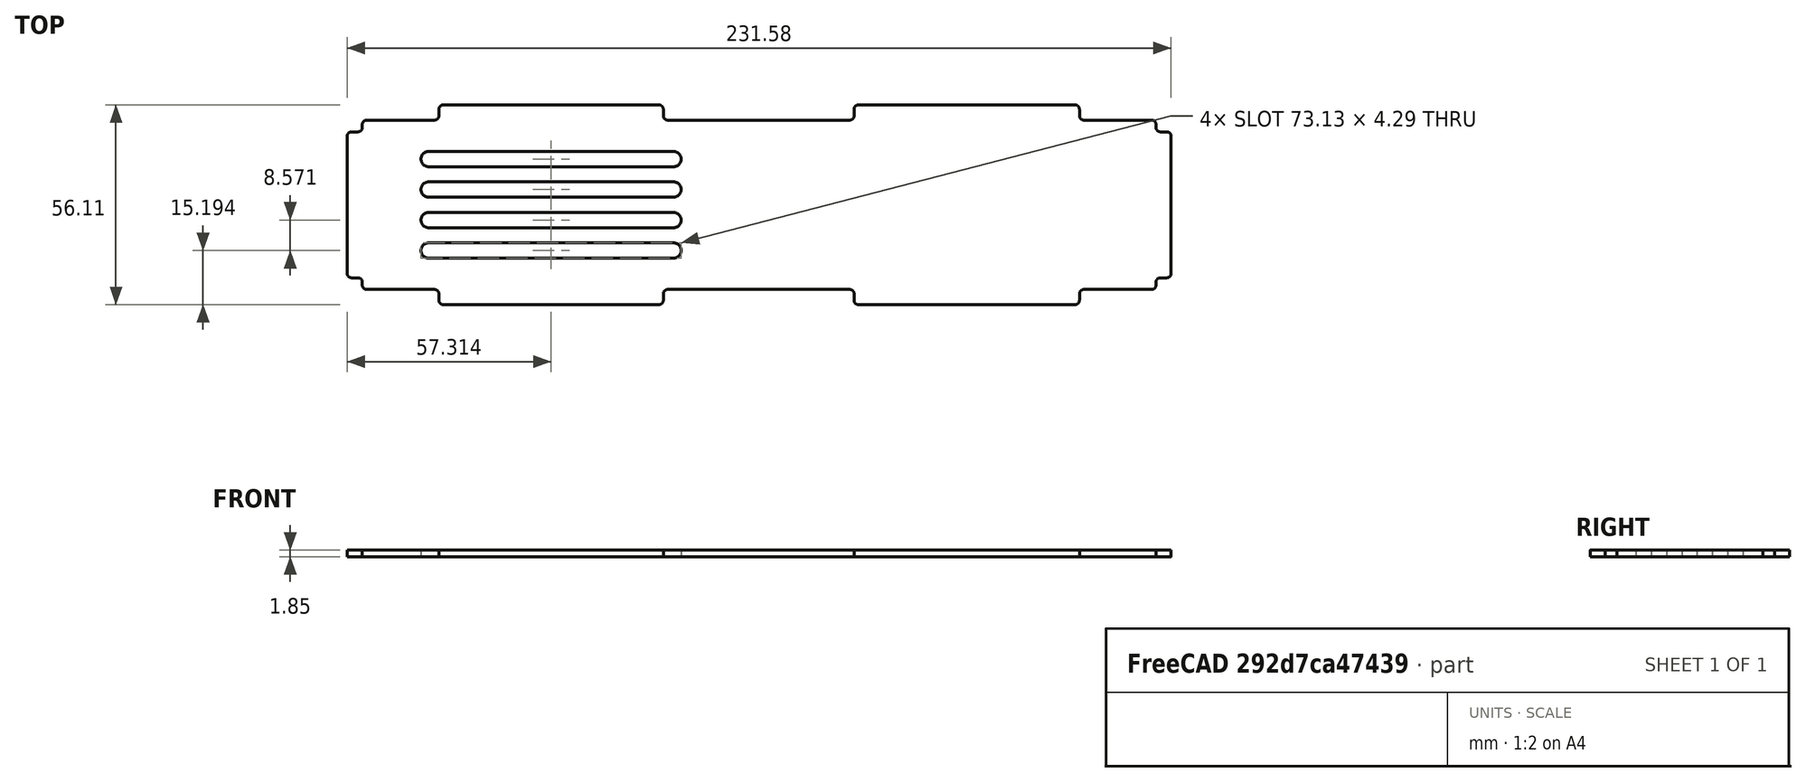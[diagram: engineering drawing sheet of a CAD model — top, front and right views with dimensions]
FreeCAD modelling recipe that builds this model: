
FCSTD DOCUMENT  (FreeCAD 1.0R38641 +468 (Git))
Label: psu_side_long
License: All rights reserved
LicenseURL: https://en.wikipedia.org/wiki/All_rights_reserved
objects: PartDesign::SubShapeBinder×2, Sketcher::SketchObject×1, PartDesign::Pad×1, PartDesign::Body×1
note: 8 computed .brp shape members not serialized (recipe doc carries the construction recipe); baked Part::Feature solids carry a one-line shape summary decoded from their .brp
EXTERNAL_REF file=../dimensions.FCStd obj=VarSet
EXTERNAL_REF file=psu_side_short.FCStd obj=Body
EXTERNAL_REF file=psu_top_and_bottom.FCStd obj=Body

FEATURE [PartDesign::SubShapeBinder] Binder  label="PsuSideShortBinderBinder"
  BindCopyOnChange = 0
  BindMode = 0
  ClaimChildren = false
  Context = -> Body [Binder.]
  Fuse = false
  MakeFace = true
  OffsetFill = false
  OffsetIntersection = false
  OffsetJoinType = 0
  OffsetOpenResult = false
  PartialLoad = false
  Placement = pos=(0.127,0,0) rot=(0,0,1;0rad)
  Refine = true
  Relative = true
  Support = -> [<external psu_side_short.FCStd>#Body]
  _Version = 2
  expr: .Placement.Base.x = dimensions#VarSet.EnclosureFinishThickness
FEATURE [PartDesign::SubShapeBinder] Binder001  label="PsuTopAndBottomBinder"
  BindCopyOnChange = 0
  BindMode = 0
  ClaimChildren = false
  Context = -> Body [Binder001.]
  Fuse = false
  MakeFace = true
  OffsetFill = false
  OffsetIntersection = false
  OffsetJoinType = 0
  OffsetOpenResult = false
  PartialLoad = false
  Refine = true
  Relative = true
  Support = -> [<external psu_top_and_bottom.FCStd>#Body]
  _Version = 2
FEATURE [Sketcher::SketchObject] Sketch
  ArcFitTolerance = 1e-06
  AttachmentSupport = -> [Binder001]
  ExternalGeometry = -> [Binder001,Binder]
  FullyConstrained = true
  MakeInternals = false
  MapMode = 5
  Placement = pos=(0,-3.1e-15,-14.1418) rot=(0,0,1;0rad)
  expr: Constraints[183] = dimensions#VarSet.EnclosureCornerRadius
  expr: Constraints[49] = dimensions#VarSet.EnclosureFinishThickness
  sketch-geometry (113):
    g0: LineSegment [constr] StartX=303.647 StartY=129.081 StartZ=0 EndX=303.52 EndY=129.081 EndZ=0
    g1: LineSegment [constr] StartX=240.305 StartY=129.081 StartZ=0 EndX=240.178 EndY=129.081 EndZ=0
    g2: LineSegment [constr] StartX=123.353 StartY=129.081 StartZ=0 EndX=123.48 EndY=129.081 EndZ=0
    g3: LineSegment [constr] StartX=186.695 StartY=129.081 StartZ=0 EndX=186.568 EndY=129.081 EndZ=0
    g4: LineSegment [constr] StartX=326.235 StartY=133.444 StartZ=0 EndX=326.235 EndY=133.571 EndZ=0
    g5: LineSegment [constr] StartX=326.235 StartY=174.719 StartZ=0 EndX=326.235 EndY=174.592 EndZ=0
    g6: LineSegment StartX=326.235 StartY=174.592 StartZ=0 EndX=328.089 EndY=174.592 EndZ=0
    g7: LineSegment StartX=329.289 StartY=173.392 StartZ=0 EndX=329.289 EndY=134.771 EndZ=0
    g8: LineSegment StartX=328.089 StartY=133.571 StartZ=0 EndX=326.235 EndY=133.571 EndZ=0
    g9: LineSegment StartX=303.52 StartY=129.081 StartZ=0 EndX=303.52 EndY=127.227 EndZ=0
    g10: LineSegment StartX=240.178 StartY=129.081 StartZ=0 EndX=240.178 EndY=127.227 EndZ=0
    g11: LineSegment StartX=241.378 StartY=126.027 StartZ=0 EndX=302.32 EndY=126.027 EndZ=0
    g12: LineSegment StartX=186.568 StartY=129.081 StartZ=0 EndX=186.568 EndY=127.227 EndZ=0
    g13: LineSegment StartX=123.48 StartY=129.081 StartZ=0 EndX=123.48 EndY=127.227 EndZ=0
    g14: LineSegment StartX=124.68 StartY=126.027 StartZ=0 EndX=185.368 EndY=126.027 EndZ=0
    g15: LineSegment StartX=240.178 StartY=179.081 StartZ=0 EndX=240.178 EndY=180.935 EndZ=0
    g16: LineSegment StartX=241.378 StartY=182.135 StartZ=0 EndX=302.32 EndY=182.135 EndZ=0
    g17: LineSegment StartX=303.52 StartY=180.935 StartZ=0 EndX=303.52 EndY=179.081 EndZ=0
    g18: LineSegment StartX=304.72 StartY=130.281 StartZ=0 EndX=323.835 EndY=130.281 EndZ=0
    g19: LineSegment StartX=325.035 StartY=131.481 StartZ=0 EndX=325.035 EndY=132.371 EndZ=0
    g20: LineSegment StartX=304.72 StartY=177.881 StartZ=0 EndX=323.835 EndY=177.881 EndZ=0
    g21: LineSegment StartX=325.035 StartY=176.681 StartZ=0 EndX=325.035 EndY=175.792 EndZ=0
    g22: LineSegment StartX=187.768 StartY=130.281 StartZ=0 EndX=238.978 EndY=130.281 EndZ=0
    g23: LineSegment StartX=122.28 StartY=130.281 StartZ=0 EndX=103.165 EndY=130.281 EndZ=0
    g24: LineSegment StartX=101.965 StartY=131.481 StartZ=0 EndX=101.965 EndY=132.371 EndZ=0
    g25: LineSegment StartX=100.765 StartY=133.571 StartZ=0 EndX=98.9106 EndY=133.571 EndZ=0
    g26: LineSegment StartX=97.7106 StartY=134.771 StartZ=0 EndX=97.7106 EndY=173.392 EndZ=0
    g27: LineSegment StartX=98.9106 StartY=174.592 StartZ=0 EndX=100.765 EndY=174.592 EndZ=0
    g28: LineSegment StartX=101.965 StartY=175.792 StartZ=0 EndX=101.965 EndY=176.681 EndZ=0
    g29: LineSegment StartX=103.165 StartY=177.881 StartZ=0 EndX=122.28 EndY=177.881 EndZ=0
    g30: LineSegment StartX=123.48 StartY=179.081 StartZ=0 EndX=123.48 EndY=180.935 EndZ=0
    g31: LineSegment StartX=124.68 StartY=182.135 StartZ=0 EndX=185.368 EndY=182.135 EndZ=0
    g32: LineSegment StartX=186.568 StartY=180.935 StartZ=0 EndX=186.568 EndY=179.081 EndZ=0
    g33: LineSegment StartX=238.978 StartY=177.881 StartZ=0 EndX=187.768 EndY=177.881 EndZ=0
    g34: ArcOfCircle CenterX=122.28 CenterY=129.081 CenterZ=0 NormalX=0 NormalY=0 NormalZ=1 AngleXU=0 Radius=1.2 StartAngle=4.2e-15 EndAngle=1.5708
    g35: ArcOfCircle CenterX=187.768 CenterY=129.081 CenterZ=0 NormalX=0 NormalY=0 NormalZ=1 AngleXU=0 Radius=1.2 StartAngle=1.5708 EndAngle=3.14159
    g36: ArcOfCircle CenterX=238.978 CenterY=129.081 CenterZ=0 NormalX=0 NormalY=0 NormalZ=1 AngleXU=0 Radius=1.2 StartAngle=2.7e-15 EndAngle=1.5708
    g37: ArcOfCircle CenterX=304.72 CenterY=129.081 CenterZ=0 NormalX=0 NormalY=0 NormalZ=1 AngleXU=0 Radius=1.2 StartAngle=1.5708 EndAngle=3.14159
    g38: ArcOfCircle CenterX=326.235 CenterY=132.371 CenterZ=0 NormalX=0 NormalY=0 NormalZ=1 AngleXU=0 Radius=1.2 StartAngle=1.5708 EndAngle=3.14159
    g39: ArcOfCircle CenterX=326.235 CenterY=175.792 CenterZ=0 NormalX=0 NormalY=0 NormalZ=1 AngleXU=0 Radius=1.2 StartAngle=3.14159 EndAngle=4.71239
    g40: ArcOfCircle CenterX=328.089 CenterY=134.771 CenterZ=0 NormalX=0 NormalY=0 NormalZ=1 AngleXU=0 Radius=1.2 StartAngle=4.71239 EndAngle=6.28319
    g41: GeomPoint [constr] X=329.289 Y=133.571 Z=0
    g42: ArcOfCircle CenterX=328.089 CenterY=173.392 CenterZ=0 NormalX=0 NormalY=0 NormalZ=1 AngleXU=0 Radius=1.2 StartAngle=1.01e-14 EndAngle=1.5708
    g43: GeomPoint [constr] X=329.289 Y=174.592 Z=0
    g44: ArcOfCircle CenterX=323.835 CenterY=176.681 CenterZ=0 NormalX=0 NormalY=0 NormalZ=1 AngleXU=0 Radius=1.2 StartAngle=1.12e-14 EndAngle=1.5708
    g45: GeomPoint [constr] X=325.035 Y=177.881 Z=0
    g46: ArcOfCircle CenterX=304.72 CenterY=179.081 CenterZ=0 NormalX=0 NormalY=0 NormalZ=1 AngleXU=0 Radius=1.2 StartAngle=3.14159 EndAngle=4.71239
    g47: GeomPoint [constr] X=303.52 Y=177.881 Z=0
    g48: ArcOfCircle CenterX=302.32 CenterY=180.935 CenterZ=0 NormalX=0 NormalY=0 NormalZ=1 AngleXU=0 Radius=1.2 StartAngle=6.9e-15 EndAngle=1.5708
    g49: GeomPoint [constr] X=303.52 Y=182.135 Z=0
    g50: ArcOfCircle CenterX=241.378 CenterY=180.935 CenterZ=0 NormalX=0 NormalY=0 NormalZ=1 AngleXU=0 Radius=1.2 StartAngle=1.5708 EndAngle=3.14159
    g51: GeomPoint [constr] X=240.178 Y=182.135 Z=0
    g52: ArcOfCircle CenterX=238.978 CenterY=179.081 CenterZ=0 NormalX=0 NormalY=0 NormalZ=1 AngleXU=0 Radius=1.2 StartAngle=4.71239 EndAngle=6.28319
    g53: GeomPoint [constr] X=240.178 Y=177.881 Z=0
    g54: ArcOfCircle CenterX=187.768 CenterY=179.081 CenterZ=0 NormalX=0 NormalY=0 NormalZ=1 AngleXU=0 Radius=1.2 StartAngle=3.14159 EndAngle=4.71239
    g55: GeomPoint [constr] X=186.568 Y=177.881 Z=0
    g56: ArcOfCircle CenterX=185.368 CenterY=180.935 CenterZ=0 NormalX=0 NormalY=0 NormalZ=1 AngleXU=0 Radius=1.2 StartAngle=-1.07e-14 EndAngle=1.5708
    g57: GeomPoint [constr] X=186.568 Y=182.135 Z=0
    g58: ArcOfCircle CenterX=124.68 CenterY=180.935 CenterZ=0 NormalX=0 NormalY=0 NormalZ=1 AngleXU=0 Radius=1.2 StartAngle=1.5708 EndAngle=3.14159
    g59: GeomPoint [constr] X=123.48 Y=182.135 Z=0
    g60: ArcOfCircle CenterX=122.28 CenterY=179.081 CenterZ=0 NormalX=0 NormalY=0 NormalZ=1 AngleXU=0 Radius=1.2 StartAngle=4.71239 EndAngle=6.28319
    g61: GeomPoint [constr] X=123.48 Y=177.881 Z=0
    g62: ArcOfCircle CenterX=103.165 CenterY=176.681 CenterZ=0 NormalX=0 NormalY=0 NormalZ=1 AngleXU=0 Radius=1.2 StartAngle=1.5708 EndAngle=3.14159
    g63: GeomPoint [constr] X=101.965 Y=177.881 Z=0
    g64: ArcOfCircle CenterX=100.765 CenterY=175.792 CenterZ=0 NormalX=0 NormalY=0 NormalZ=1 AngleXU=0 Radius=1.2 StartAngle=4.71239 EndAngle=6.28319
    g65: GeomPoint [constr] X=101.965 Y=174.592 Z=0
    g66: ArcOfCircle CenterX=98.9106 CenterY=173.392 CenterZ=0 NormalX=0 NormalY=0 NormalZ=1 AngleXU=0 Radius=1.2 StartAngle=1.5708 EndAngle=3.14159
    g67: GeomPoint [constr] X=97.7106 Y=174.592 Z=0
    g68: ArcOfCircle CenterX=98.9106 CenterY=134.771 CenterZ=0 NormalX=0 NormalY=0 NormalZ=1 AngleXU=0 Radius=1.2 StartAngle=3.14159 EndAngle=4.71239
    g69: GeomPoint [constr] X=97.7106 Y=133.571 Z=0
    g70: ArcOfCircle CenterX=100.765 CenterY=132.371 CenterZ=0 NormalX=0 NormalY=0 NormalZ=1 AngleXU=0 Radius=1.2 StartAngle=-8e-15 EndAngle=1.5708
    g71: GeomPoint [constr] X=101.965 Y=133.571 Z=0
    g72: ArcOfCircle CenterX=103.165 CenterY=131.481 CenterZ=0 NormalX=0 NormalY=0 NormalZ=1 AngleXU=0 Radius=1.2 StartAngle=3.14159 EndAngle=4.71239
    g73: GeomPoint [constr] X=101.965 Y=130.281 Z=0
    g74: ArcOfCircle CenterX=124.68 CenterY=127.227 CenterZ=0 NormalX=0 NormalY=0 NormalZ=1 AngleXU=0 Radius=1.2 StartAngle=3.14159 EndAngle=4.71239
    g75: GeomPoint [constr] X=123.48 Y=126.027 Z=0
    g76: ArcOfCircle CenterX=185.368 CenterY=127.227 CenterZ=0 NormalX=0 NormalY=0 NormalZ=1 AngleXU=0 Radius=1.2 StartAngle=4.71239 EndAngle=6.28319
    g77: GeomPoint [constr] X=186.568 Y=126.027 Z=0
    g78: ArcOfCircle CenterX=241.378 CenterY=127.227 CenterZ=0 NormalX=0 NormalY=0 NormalZ=1 AngleXU=0 Radius=1.2 StartAngle=3.14159 EndAngle=4.71239
    g79: GeomPoint [constr] X=240.178 Y=126.027 Z=0
    g80: ArcOfCircle CenterX=302.32 CenterY=127.227 CenterZ=0 NormalX=0 NormalY=0 NormalZ=1 AngleXU=0 Radius=1.2 StartAngle=4.71239 EndAngle=6.28319
    g81: GeomPoint [constr] X=303.52 Y=126.027 Z=0
    g82: ArcOfCircle CenterX=323.835 CenterY=131.481 CenterZ=0 NormalX=0 NormalY=0 NormalZ=1 AngleXU=0 Radius=1.2 StartAngle=4.71239 EndAngle=6.28319
    g83: GeomPoint [constr] X=325.035 Y=130.281 Z=0
    g84: LineSegment [constr] StartX=120.6 StartY=129.081 StartZ=0 EndX=120.6 EndY=126.027 EndZ=0
    g85: LineSegment [constr] StartX=120.6 StartY=126.027 StartZ=0 EndX=124.68 EndY=126.027 EndZ=0
    g86: LineSegment [constr] StartX=185.368 StartY=126.027 StartZ=0 EndX=189.448 EndY=126.027 EndZ=0
    g87: LineSegment [constr] StartX=189.448 StartY=126.027 StartZ=0 EndX=189.448 EndY=139.081 EndZ=0
    g88: LineSegment [constr] StartX=120.6 StartY=129.081 StartZ=0 EndX=120.6 EndY=139.081 EndZ=0
    g89: ArcOfCircle CenterX=120.6 CenterY=141.224 CenterZ=0 NormalX=0 NormalY=0 NormalZ=1 AngleXU=0 Radius=2.14286 StartAngle=1.5708 EndAngle=4.71239
    g90: ArcOfCircle CenterX=189.448 CenterY=141.224 CenterZ=0 NormalX=0 NormalY=0 NormalZ=1 AngleXU=0 Radius=2.14286 StartAngle=4.71239 EndAngle=7.85398
    g91: LineSegment StartX=120.6 StartY=143.367 StartZ=0 EndX=189.448 EndY=143.367 EndZ=0
    g92: LineSegment StartX=120.6 StartY=139.081 StartZ=0 EndX=189.448 EndY=139.081 EndZ=0
    g93: ArcOfCircle CenterX=120.6 CenterY=149.796 CenterZ=0 NormalX=0 NormalY=0 NormalZ=1 AngleXU=0 Radius=2.14286 StartAngle=1.5708 EndAngle=4.71239
    g94: ArcOfCircle CenterX=189.448 CenterY=149.796 CenterZ=0 NormalX=0 NormalY=0 NormalZ=1 AngleXU=0 Radius=2.14286 StartAngle=4.71239 EndAngle=7.85398
    g95: LineSegment StartX=120.6 StartY=151.938 StartZ=0 EndX=189.448 EndY=151.938 EndZ=0
    g96: LineSegment StartX=120.6 StartY=147.653 StartZ=0 EndX=189.448 EndY=147.653 EndZ=0
    g97: LineSegment [constr] StartX=120.6 StartY=139.081 StartZ=0 EndX=120.6 EndY=143.367 EndZ=0
    g98: LineSegment [constr] StartX=120.6 StartY=143.367 StartZ=0 EndX=120.6 EndY=147.653 EndZ=0
    g99: LineSegment [constr] StartX=120.6 StartY=147.653 StartZ=0 EndX=120.6 EndY=151.938 EndZ=0
    g100: LineSegment [constr] StartX=120.6 StartY=151.938 StartZ=0 EndX=120.6 EndY=156.224 EndZ=0
    g101: LineSegment [constr] StartX=120.6 StartY=156.224 StartZ=0 EndX=120.6 EndY=160.51 EndZ=0
    g102: LineSegment [constr] StartX=120.6 StartY=160.51 StartZ=0 EndX=120.6 EndY=164.796 EndZ=0
    g103: LineSegment [constr] StartX=120.6 StartY=164.796 StartZ=0 EndX=120.6 EndY=169.081 EndZ=0
    g104: ArcOfCircle CenterX=120.6 CenterY=158.367 CenterZ=0 NormalX=0 NormalY=0 NormalZ=1 AngleXU=0 Radius=2.14286 StartAngle=1.5708 EndAngle=4.71239
    g105: ArcOfCircle CenterX=189.448 CenterY=158.367 CenterZ=0 NormalX=0 NormalY=0 NormalZ=1 AngleXU=0 Radius=2.14286 StartAngle=4.71239 EndAngle=7.85398
    g106: LineSegment StartX=120.6 StartY=160.51 StartZ=0 EndX=189.448 EndY=160.51 EndZ=0
    g107: LineSegment StartX=120.6 StartY=156.224 StartZ=0 EndX=189.448 EndY=156.224 EndZ=0
    g108: ArcOfCircle CenterX=120.6 CenterY=166.938 CenterZ=0 NormalX=0 NormalY=0 NormalZ=1 AngleXU=0 Radius=2.14286 StartAngle=1.5708 EndAngle=4.71239
    g109: ArcOfCircle CenterX=189.448 CenterY=166.938 CenterZ=0 NormalX=0 NormalY=0 NormalZ=1 AngleXU=0 Radius=2.14286 StartAngle=4.71239 EndAngle=7.85398
    g110: LineSegment StartX=120.6 StartY=169.081 StartZ=0 EndX=189.448 EndY=169.081 EndZ=0
    g111: LineSegment StartX=120.6 StartY=164.796 StartZ=0 EndX=189.448 EndY=164.796 EndZ=0
    g112: LineSegment [constr] StartX=189.448 StartY=139.081 StartZ=0 EndX=189.448 EndY=169.081 EndZ=0
  constraints (266):
    c: Coincident(g0,g-4)
    c: PointOnObject(g0,g-4)
    c: Coincident(g1,g-4)
    c: Coincident(g2,g-3)
    c: Coincident(g3,g-3)
    c: Coincident(g4,g-5)
    c: PointOnObject(g4,g-5)
    c: Coincident(g5,g-5)
    c: PointOnObject(g5,g-5)
    c: Equal(g4,g5)
    c: Equal(g0,g4)
    c: Equal(g0,g1)
    c: Equal(g1,g3)
    c: Equal(g3,g2)
    c: Horizontal(g6)
    c: Vertical(g7)
    c: Horizontal(g8)
    c: Vertical(g9)
    c: Horizontal(g11)
    c: Vertical(g13)
    c: Horizontal(g14)
    c: Vertical(g15)
    c: Horizontal(g16)
    c: Vertical(g17)
    c: Horizontal(g18)
    c: Vertical(g19)
    c: Horizontal(g20)
    c: Vertical(g21)
    c: Horizontal(g23)
    c: Vertical(g24)
    c: Horizontal(g25)
    c: Vertical(g26)
    c: Horizontal(g27)
    c: Vertical(g28)
    c: Horizontal(g29)
    c: Vertical(g30)
    c: Horizontal(g31)
    c: Vertical(g32)
    c: Horizontal(g33)
    c: Tangent(g34,g23) = -1.5708
    c: Tangent(g37,g18) = 1.5708
    c: Tangent(g9,g37) = -1.5708
    c: Coincident(g9,g0)
    c: Tangent(g38,g8) = -1.5708
    c: Coincident(g8,g4)
    c: Tangent(g19,g38) = 1.5708
    c: Tangent(g6,g39) = -1.5708
    c: Coincident(g5,g6)
    c: Tangent(g39,g21) = -1.5708
    c: DistanceY(g4,g4) = 0.127
    c: PointOnObject(g41,g7)
    c: PointOnObject(g41,g8)
    c: Tangent(g7,g40) = 1.5708
    c: Tangent(g8,g40) = 1.5708
    c: PointOnObject(g43,g6)
    c: PointOnObject(g43,g7)
    c: Tangent(g6,g42) = 1.5708
    c: Tangent(g7,g42) = 1.5708
    c: PointOnObject(g45,g20)
    c: PointOnObject(g45,g21)
    c: Tangent(g20,g44) = 1.5708
    c: Tangent(g21,g44) = 1.5708
    c: PointOnObject(g47,g17)
    c: PointOnObject(g47,g20)
    c: Tangent(g17,g46) = -1.5708
    c: Tangent(g20,g46) = -1.5708
    c: PointOnObject(g49,g16)
    c: PointOnObject(g49,g17)
    c: Tangent(g16,g48) = 1.5708
    c: Tangent(g17,g48) = 1.5708
    c: PointOnObject(g51,g15)
    c: PointOnObject(g51,g16)
    c: Tangent(g15,g50) = 1.5708
    c: Tangent(g16,g50) = 1.5708
    c: PointOnObject(g53,g15)
    c: PointOnObject(g53,g33)
    c: Tangent(g15,g52) = -1.5708
    c: Tangent(g33,g52) = 1.5708
    c: PointOnObject(g55,g32)
    c: PointOnObject(g55,g33)
    c: Tangent(g32,g54) = -1.5708
    c: Tangent(g33,g54) = 1.5708
    c: PointOnObject(g57,g31)
    c: PointOnObject(g57,g32)
    c: Tangent(g31,g56) = 1.5708
    c: Tangent(g32,g56) = 1.5708
    c: PointOnObject(g59,g30)
    c: PointOnObject(g59,g31)
    c: Tangent(g30,g58) = 1.5708
    c: Tangent(g31,g58) = 1.5708
    c: PointOnObject(g61,g29)
    c: PointOnObject(g61,g30)
    c: Tangent(g29,g60) = -1.5708
    c: Tangent(g30,g60) = -1.5708
    c: PointOnObject(g63,g28)
    c: PointOnObject(g63,g29)
    c: Tangent(g28,g62) = 1.5708
    c: Tangent(g29,g62) = 1.5708
    c: PointOnObject(g65,g27)
    c: PointOnObject(g65,g28)
    c: Tangent(g27,g64) = -1.5708
    c: Tangent(g28,g64) = -1.5708
    c: PointOnObject(g67,g26)
    c: PointOnObject(g67,g27)
    c: Tangent(g26,g66) = 1.5708
    c: Tangent(g27,g66) = 1.5708
    c: PointOnObject(g69,g25)
    c: PointOnObject(g69,g26)
    c: Tangent(g25,g68) = 1.5708
    c: Tangent(g26,g68) = 1.5708
    c: PointOnObject(g71,g24)
    c: PointOnObject(g71,g25)
    c: Tangent(g24,g70) = -1.5708
    c: Tangent(g25,g70) = -1.5708
    c: PointOnObject(g73,g23)
    c: PointOnObject(g73,g24)
    c: Tangent(g23,g72) = 1.5708
    c: Tangent(g24,g72) = 1.5708
    c: PointOnObject(g75,g13)
    c: PointOnObject(g75,g14)
    c: Tangent(g13,g74) = -1.5708
    c: Tangent(g14,g74) = -1.5708
    c: PointOnObject(g77,g12)
    c: PointOnObject(g77,g14)
    c: Tangent(g12,g76) = 1.5708
    c: Tangent(g14,g76) = -1.5708
    c: PointOnObject(g79,g10)
    c: PointOnObject(g79,g11)
    c: Tangent(g10,g78) = -1.5708
    c: Tangent(g11,g78) = -1.5708
    c: PointOnObject(g81,g9)
    c: PointOnObject(g81,g11)
    c: Tangent(g9,g80) = 1.5708
    c: Tangent(g11,g80) = -1.5708
    c: PointOnObject(g83,g18)
    c: PointOnObject(g83,g19)
    c: Tangent(g18,g82) = -1.5708
    c: Tangent(g19,g82) = -1.5708
    c: Equal(g34,g35)
    c: Equal(g36,g37)
    c: Equal(g37,g38)
    c: Equal(g38,g39)
    c: Equal(g39,g40)
    c: Equal(g40,g42)
    c: Equal(g42,g44)
    c: Equal(g44,g46)
    c: Equal(g46,g48)
    c: Equal(g48,g50)
    c: Equal(g50,g52)
    c: Equal(g52,g54)
    c: Equal(g54,g56)
    c: Equal(g56,g58)
    c: Equal(g58,g60)
    c: Equal(g60,g62)
    c: Equal(g62,g64)
    c: Equal(g64,g66)
    c: Equal(g66,g68)
    c: Equal(g68,g70)
    c: Equal(g70,g72)
    c: Equal(g72,g74)
    c: Equal(g74,g76)
    c: Equal(g76,g78)
    c: Equal(g78,g80)
    c: Equal(g80,g82)
    c: Tangent(g35,g12) = -1.5708
    c: Tangent(g35,g22) = 1.5708
    c: Coincident(g12,g3)
    c: PointOnObject(g3,g-3)
    c: PointOnObject(g2,g-3)
    c: PointOnObject(g1,g-4)
    c: Tangent(g36,g10) = 1.5708
    c: Coincident(g10,g1)
    c: Tangent(g36,g22) = 1.5708
    c: Vertical(g10)
    c: Vertical(g12)
    c: Horizontal(g22)
    c: Tangent(g34,g13) = 1.5708
    c: Coincident(g13,g2)
    c: Equal(g31,g14)
    c: Equal(g22,g33)
    c: Equal(g11,g16)
    c: Equal(g18,g20)
    c: Equal(g21,g19)
    c: Radius(g38) = 1.2
    c: Equal(g9,g17)
    c: PointOnObject(g9,g-7)
    c: Equal(g10,g15)
    c: PointOnObject(g12,g-8)
    c: Equal(g12,g32)
    c: Equal(g30,g13)
    c: Equal(g23,g29)
    c: Equal(g24,g19)
    c: Equal(g21,g28)
    c: Equal(g23,g18)
    c: Equal(g27,g6)
    c: PointOnObject(g6,g-6)
    c: Vertical(g84)
    c: Coincident(g85,g84)
    c: Horizontal(g85)
    c: Coincident(g85,g14)
    c: Coincident(g86,g14)
    c: Horizontal(g86)
    c: Coincident(g87,g86)
    c: Vertical(g87)
    c: Equal(g86,g85)
    c: Coincident(g-9,g84)
    c: Coincident(g88,g84)
    c: Vertical(g88)
    c: Tangent(g89,g91) = 1.5708
    c: Tangent(g89,g92) = -1.5708
    c: Tangent(g90,g91) = 1.5708
    c: Tangent(g90,g92) = -1.5708
    c: Equal(g89,g90)
    c: Horizontal(g91)
    c: Tangent(g93,g95) = 1.5708
    c: Tangent(g93,g96) = -1.5708
    c: Tangent(g94,g95) = 1.5708
    c: Tangent(g94,g96) = -1.5708
    c: Equal(g93,g94)
    c: Horizontal(g95)
    c: Coincident(g97,g89)
    c: Coincident(g97,g89)
    c: Coincident(g98,g89)
    c: Coincident(g98,g93)
    c: Coincident(g99,g93)
    c: Coincident(g99,g93)
    c: Coincident(g100,g93)
    c: Vertical(g100)
    c: Equal(g97,g98)
    c: Vertical(g98)
    c: Equal(g99,g98)
    c: Equal(g100,g99)
    c: Vertical(g101)
    c: Coincident(g102,g101)
    c: Vertical(g102)
    c: Coincident(g103,g102)
    c: Vertical(g103)
    c: Coincident(g90,g87)
    c: Tangent(g104,g106) = 1.5708
    c: Tangent(g104,g107) = -1.5708
    c: Tangent(g105,g106) = 1.5708
    c: Tangent(g105,g107) = -1.5708
    c: Coincident(g101,g104)
    c: Coincident(g100,g101)
    c: Coincident(g100,g104)
    c: Horizontal(g106)
    c: Tangent(g108,g110) = 1.5708
    c: Tangent(g108,g111) = -1.5708
    c: Tangent(g109,g110) = 1.5708
    c: Tangent(g109,g111) = -1.5708
    c: Equal(g108,g109)
    c: Equal(g101,g100)
    c: Equal(g102,g101)
    c: Equal(g102,g103)
    c: Coincident(g102,g108)
    c: Coincident(g108,g103)
    c: Coincident(g112,g87)
    c: Vertical(g112)
    c: Coincident(g109,g112)
    c: PointOnObject(g105,g112)
    c: PointOnObject(g94,g112)
    c: Coincident(g88,g89)
    c: DistanceY(g88,g88) = 10
    c: DistanceY(g84,g103) = 40
    c: Distance(g31,g110) = 13.0542
    c: Distance(g14,g92) = 13.0542
FEATURE [PartDesign::Pad] Pad
  Direction = (0,0,1)
  Length = 1.8542
  Length2 = 10
  Profile = -> Sketch
  ReferenceAxis = -> Sketch [N_Axis]
  Refine = true
  Suppressed = false
  Type = 0
  expr: Length = dimensions#VarSet.EnclosureTotalThickness
FEATURE [PartDesign::Body] Body  label="PsuSideLong"
  AllowCompound = false
  Group = -> [Binder,Binder001,Sketch,Pad]
  Origin = -> Origin
  Tip = -> Pad
